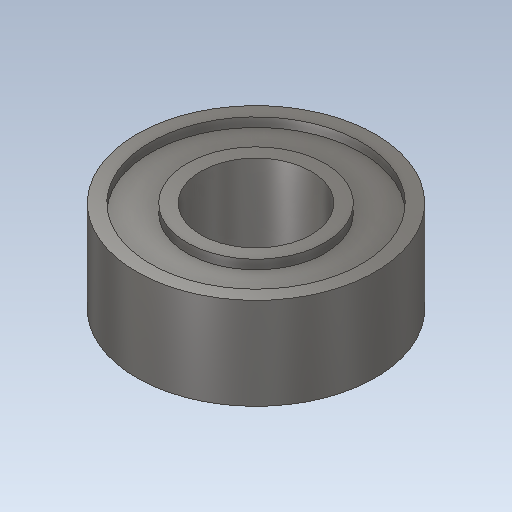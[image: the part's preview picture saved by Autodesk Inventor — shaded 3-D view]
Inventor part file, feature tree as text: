
AUTODESK INVENTOR PART (.ipt)
format: ipt  version: 2020 (Build 240168000, 168)  size: 162,816 bytes
history: native  units: mm
features: extrude x3, sketch x3, projected_geometry x2
ambient origin geometry x8: Origin, YZ Plane, XZ Plane, XY Plane, X Axis, Y Axis, Z Axis, Center Point
bodies: 实体1 (feature_tree)
feature tree (8):
  extrude  "拉伸1"  Depth=6.0mm
  extrude  "拉伸2"  Depth=5.0mm
  extrude  "拉伸3"  Depth=0.5mm TaperAngle=0.0deg
  sketch  "草图1"  dims[d0=13.0mm d1=6.0mm]
  sketch  "草图2"  dims[d2=5.0mm d3=0.0mm d4=11.5mm]
  projected_geometry  "投影回路1"
  sketch  "草图3"  dims[d5=7.5mm d6=0.5mm d7=0.0mm d8=0.5mm d9=0.0mm]
  projected_geometry  "投影回路2"
